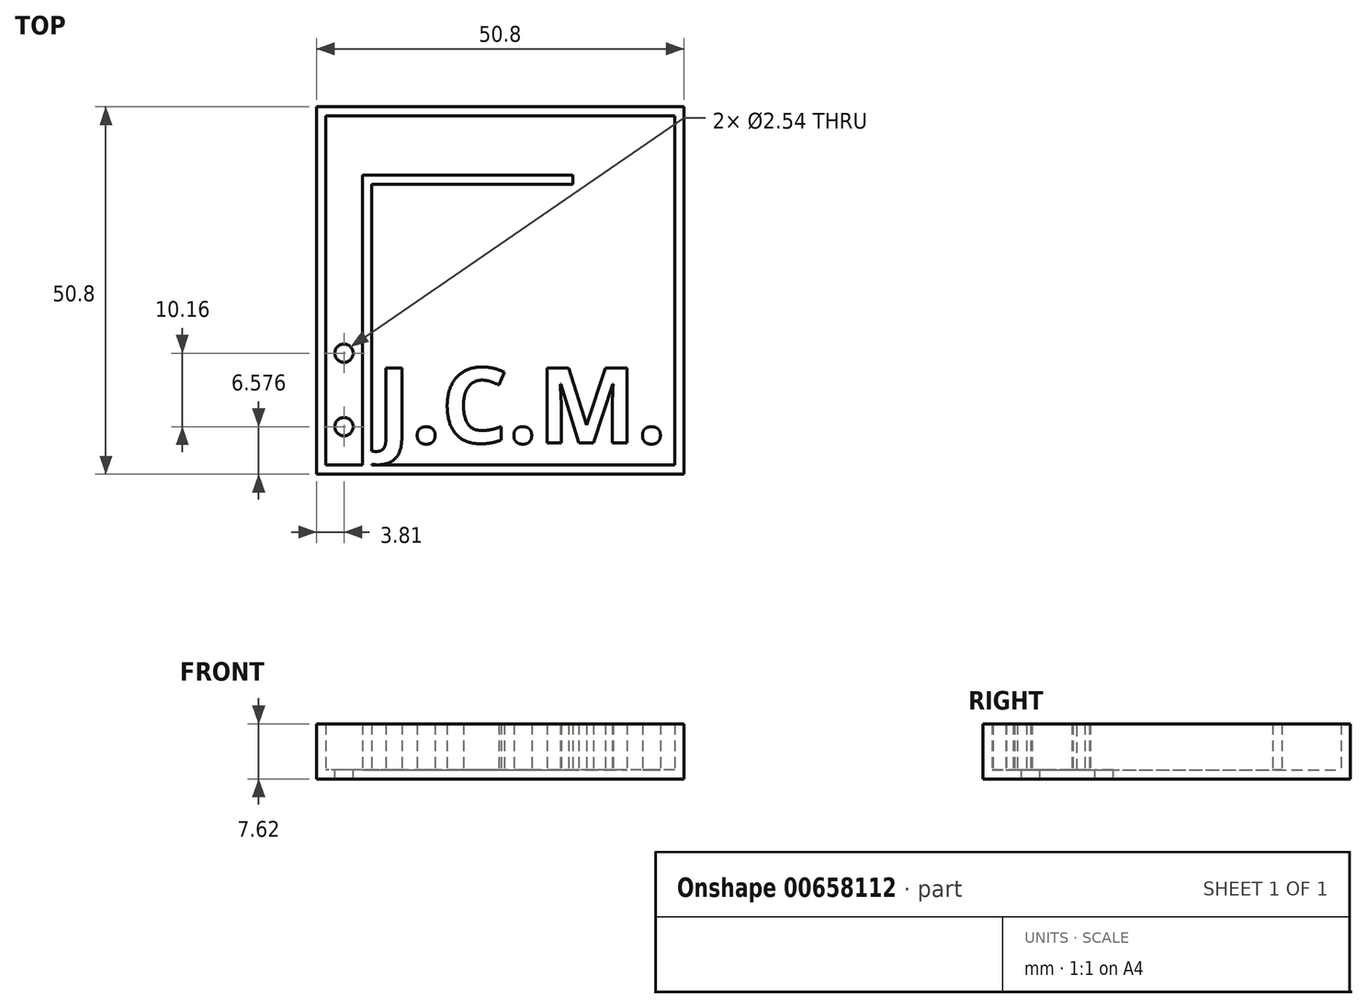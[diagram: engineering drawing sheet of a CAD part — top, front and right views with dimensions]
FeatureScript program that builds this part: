
annotation { "Feature Type Name" : "Feature", "Feature Type Description" : "" }
export const myFeature = defineFeature(function(context is Context, id is Id, definition is map)
    precondition{}
    {
        {
            var Q0;
            Q0=qCreatedBy(makeId("Top.planeOp"),FACE);
            var sketch = newSketch(context, id + "F0", { "sketchPlane" : qUnion([Q0])});
            skLineSegment(sketch, "E0.bottom", {"start": v(0, 0) * mm, "end": v(-50.8, 0) * mm});
            skLineSegment(sketch, "E0.top", {"start": v(0, 50.8) * mm, "end": v(-50.8, 50.8) * mm});
            skLineSegment(sketch, "E0.left", {"start": v(0, 0) * mm, "end": v(0, 50.8) * mm});
            skLineSegment(sketch, "E0.right", {"start": v(-50.8, 0) * mm, "end": v(-50.8, 50.8) * mm});
            skSolve(sketch);
        }
        {
            var Q0;
            Q0 = qSketchRegion(id + "F0", true);
            extrude(context, id + "F1", {"entities" : qUnion([Q0]), "depth" : 7.62 * mm, "offsetDistance" : 25.4 * mm});
        }
        {
            var Q0;
            Q0=makeQuery(id+"F1.opExtrude","CAP_FACE",FACE,{"disambiguationData":[OSD([sQuery(id+"F0.wireOp",EDGE,"E0.bottom"),sQuery(id+"F0.wireOp",EDGE,"E0.top"),sQuery(id+"F0.wireOp",EDGE,"E0.left"),sQuery(id+"F0.wireOp",EDGE,"E0.right")])],"isStart":false});
            shell(context, id + "F2", {"entities" : qUnion([Q0]), "thickness" : 1.27 * mm});
        }
        {
            var Q0;
            Q0=makeQuery(id+"F2.opShell","OFFSET_FACE",FACE,{"disambiguationData":[OSD([sQuery(id+"F0.wireOp",EDGE,"E0.bottom"),sQuery(id+"F0.wireOp",EDGE,"E0.top"),sQuery(id+"F0.wireOp",EDGE,"E0.left"),sQuery(id+"F0.wireOp",EDGE,"E0.right")])]});
            var sketch = newSketch(context, id + "F3", { "sketchPlane" : qUnion([Q0])});
            skLineSegment(sketch, "E1", {"start": v(-49.53, 1.27) * mm, "end": v(-44.45, 1.27) * mm});
            skLineSegment(sketch, "E2.bottom", {"start": v(-44.45, 1.27) * mm, "end": v(-43.18, 1.27) * mm});
            skLineSegment(sketch, "E2.top", {"start": v(-44.45, 41.34) * mm, "end": v(-43.18, 41.34) * mm});
            skLineSegment(sketch, "E2.left", {"start": v(-44.45, 1.27) * mm, "end": v(-44.45, 41.34) * mm});
            skLineSegment(sketch, "E2.right", {"start": v(-43.18, 1.27) * mm, "end": v(-43.18, 41.34) * mm});
            skSolve(sketch);
        }
        {
            var Q0;
            Q0=makeQuery(id+"F3.imprint","IMPRINT",FACE,{"disambiguationData":[TD([[makeQuery(id+"F3.imprint","IMPRINT",EDGE,{"derivedFrom":sQuery(id+"F3.wireOp",EDGE,"E2.bottom")}),-1.0]])]});
            extrude(context, id + "F4", {"entities" : qUnion([Q0]), "operationType" : NewBodyOperationType.ADD, "depth" : 6.35 * mm, "offsetDistance" : 25.4 * mm});
        }
        {
            var Q0;
            Q0=makeQuery(id+"F2.opShell","OFFSET_FACE",FACE,{"disambiguationData":[OSD([sQuery(id+"F0.wireOp",EDGE,"E0.bottom"),sQuery(id+"F0.wireOp",EDGE,"E0.top"),sQuery(id+"F0.wireOp",EDGE,"E0.left"),sQuery(id+"F0.wireOp",EDGE,"E0.right")])]});
            var sketch = newSketch(context, id + "F5", { "sketchPlane" : qUnion([Q0])});
            skCircle(sketch, "E3", {"center": v(-47, 6.58) * mm, "radius": 1.27 * mm});
            skSolve(sketch);
        }
        {
            var Q0;
            Q0=makeQuery(id+"F5.imprint","IMPRINT",FACE,{"disambiguationData":[TD([[makeQuery(id+"F5.imprint","IMPRINT",EDGE,{"derivedFrom":sQuery(id+"F5.wireOp",EDGE,"E3")}),1.0]])]});
            extrude(context, id + "F6", {"entities" : qUnion([Q0]), "operationType" : NewBodyOperationType.REMOVE, "oppositeDirection" : true, "depth" : 25.4 * mm, "offsetDistance" : 25.4 * mm});
        }
        {
            var Q0;
            Q0=makeQuery(id+"F2.opShell","OFFSET_FACE",FACE,{"disambiguationData":[OSD([sQuery(id+"F0.wireOp",EDGE,"E0.bottom"),sQuery(id+"F0.wireOp",EDGE,"E0.top"),sQuery(id+"F0.wireOp",EDGE,"E0.left"),sQuery(id+"F0.wireOp",EDGE,"E0.right")])]});
            var sketch = newSketch(context, id + "F7", { "sketchPlane" : qUnion([Q0])});
            skCircle(sketch, "E4", {"center": v(-47, 16.74) * mm, "radius": 1.27 * mm});
            skSolve(sketch);
        }
        {
            var Q0;
            Q0=makeQuery(id+"F7.imprint","IMPRINT",FACE,{"disambiguationData":[TD([[makeQuery(id+"F7.imprint","IMPRINT",EDGE,{"derivedFrom":sQuery(id+"F7.wireOp",EDGE,"E4")}),1.0]])]});
            extrude(context, id + "F8", {"entities" : qUnion([Q0]), "operationType" : NewBodyOperationType.REMOVE, "oppositeDirection" : true, "depth" : 25.4 * mm, "offsetDistance" : 25.4 * mm});
        }
        {
            var Q0;
            Q0=makeQuery(id+"F2.opShell","OFFSET_FACE",FACE,{"disambiguationData":[OSD([sQuery(id+"F0.wireOp",EDGE,"E0.bottom"),sQuery(id+"F0.wireOp",EDGE,"E0.top"),sQuery(id+"F0.wireOp",EDGE,"E0.left"),sQuery(id+"F0.wireOp",EDGE,"E0.right")])]});
            var sketch = newSketch(context, id + "F9", { "sketchPlane" : qUnion([Q0])});
            skLineSegment(sketch, "E5.bottom", {"start": v(-43.18, 41.34) * mm, "end": v(-15.37, 41.34) * mm});
            skLineSegment(sketch, "E5.top", {"start": v(-43.18, 40.07) * mm, "end": v(-15.37, 40.07) * mm});
            skLineSegment(sketch, "E5.left", {"start": v(-43.18, 41.34) * mm, "end": v(-43.18, 40.07) * mm});
            skLineSegment(sketch, "E5.right", {"start": v(-15.37, 41.34) * mm, "end": v(-15.37, 40.07) * mm});
            skLineSegment(sketch, "E6.bottom", {"start": v(-15.37, 40.07) * mm, "end": v(-16.64, 40.07) * mm});
            skLineSegment(sketch, "E6.top", {"start": v(-15.37, 33.74) * mm, "end": v(-16.64, 33.74) * mm});
            skLineSegment(sketch, "E6.left", {"start": v(-15.37, 40.07) * mm, "end": v(-15.37, 33.74) * mm});
            skLineSegment(sketch, "E6.right", {"start": v(-16.64, 40.07) * mm, "end": v(-16.64, 33.74) * mm});
            skSolve(sketch);
        }
        {
            var Q0;
            Q0=makeQuery(id+"F9.imprint","IMPRINT",FACE,{"disambiguationData":[TD([[makeQuery(id+"F9.imprint","IMPRINT",EDGE,{"derivedFrom":sQuery(id+"F9.wireOp",EDGE,"E5.bottom")}),-1.0]])]});
            var Q1;
            Q1=makeQuery(id+"F9.imprint","IMPRINT",FACE,{"disambiguationData":[TD([[makeQuery(id+"F9.imprint","IMPRINT",EDGE,{"derivedFrom":sQuery(id+"F9.wireOp",EDGE,"E6.bottom")}),1.0]])]});
            extrude(context, id + "F10", {"entities" : qUnion([Q0, Q1]), "operationType" : NewBodyOperationType.ADD, "depth" : 6.35 * mm, "offsetDistance" : 25.4 * mm});
        }
        {
            var Q0;
            Q0=makeQuery(id+"F2.opShell","OFFSET_FACE",FACE,{"disambiguationData":[OSD([sQuery(id+"F0.wireOp",EDGE,"E0.bottom"),sQuery(id+"F0.wireOp",EDGE,"E0.top"),sQuery(id+"F0.wireOp",EDGE,"E0.left"),sQuery(id+"F0.wireOp",EDGE,"E0.right")])]});
            var sketch = newSketch(context, id + "F11", { "sketchPlane" : qUnion([Q0])});
            skText(sketch, "E7", { "text": "J.C.M.", "fontName": "OpenSans-Bold.ttf"});
            const initialGuessF11  = {"E7": [-0.0425, 0.00435, 1, 0, 0.01043]};
            skSetInitialGuess(sketch, initialGuessF11);
            skSolve(sketch);
        }
        {
            var Q0;
            Q0 = qSketchRegion(id + "F11", true);
            extrude(context, id + "F12", {"entities" : qUnion([Q0]), "operationType" : NewBodyOperationType.ADD, "depth" : 6.35 * mm, "offsetDistance" : 25.4 * mm});
        }
    });
